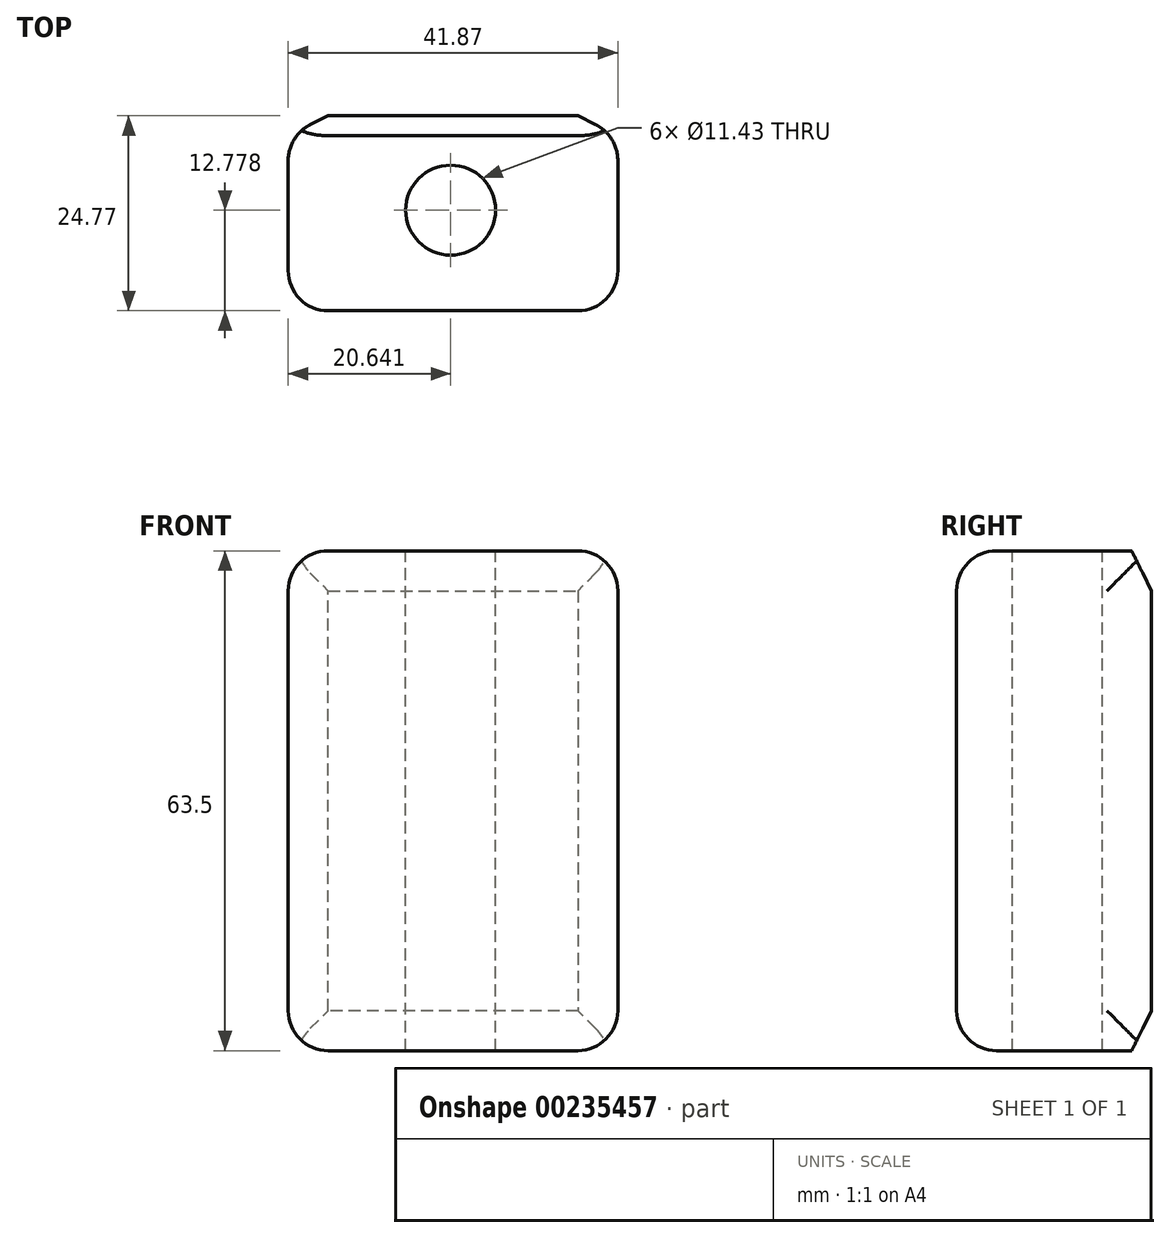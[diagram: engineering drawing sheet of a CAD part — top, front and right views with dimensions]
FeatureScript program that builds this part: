
annotation { "Feature Type Name" : "Feature", "Feature Type Description" : "" }
export const myFeature = defineFeature(function(context is Context, id is Id, definition is map)
    precondition{}
    {
        {
            var Q0;
            Q0=qCreatedBy(makeId("Top.planeOp"),FACE);
            var sketch = newSketch(context, id + "F0", { "sketchPlane" : qUnion([Q0])});
            skLineSegment(sketch, "E0.bottom", {"start": v(0, 0) * mm, "end": v(41.87, 0) * mm});
            skLineSegment(sketch, "E0.top", {"start": v(0, 24.77) * mm, "end": v(41.87, 24.77) * mm});
            skLineSegment(sketch, "E0.left", {"start": v(0, 0) * mm, "end": v(0, 24.77) * mm});
            skLineSegment(sketch, "E0.right", {"start": v(41.87, 0) * mm, "end": v(41.87, 24.77) * mm});
            skSolve(sketch);
        }
        {
            var Q0;
            Q0 = qSketchRegion(id + "F0", true);
            extrude(context, id + "F1", {"entities" : qUnion([Q0]), "depth" : 63.5 * mm});
        }
        {
            var Q0;
            Q0=makeQuery(id+"F1.opExtrude","CAP_FACE",FACE,{"disambiguationData":[OSD([sQuery(id+"F0.wireOp",EDGE,"E0.bottom"),sQuery(id+"F0.wireOp",EDGE,"E0.top"),sQuery(id+"F0.wireOp",EDGE,"E0.left"),sQuery(id+"F0.wireOp",EDGE,"E0.right")])],"isStart":false});
            var sketch = newSketch(context, id + "F2", { "sketchPlane" : qUnion([Q0])});
            skCircle(sketch, "E1", {"center": v(20.64, 12.78) * mm, "radius": 6.65 * mm});
            skSolve(sketch);
        }
        {
            var Q0;
            Q0=sQuery(id+"F2.wireOp",VERTEX,"E1.center");
            var Q1;
            Q1=makeQuery(id+"F1.opExtrude","SWEPT_BODY",BODY,{"disambiguationData":[OSD([sQuery(id+"F0.wireOp",EDGE,"E0.bottom"),sQuery(id+"F0.wireOp",EDGE,"E0.top"),sQuery(id+"F0.wireOp",EDGE,"E0.left"),sQuery(id+"F0.wireOp",EDGE,"E0.right")])]});
            hole(context, id + "F3", {"style" : HoleStyle.SIMPLE, "endStyle" : HoleEndStyle.THROUGH, "holeDiameter" : 11.43 * mm, "locations" : qUnion([Q0]), "scope" : qUnion([Q1]), "isTappedThrough" : true});
        }
        {
            var Q0;
            Q0=makeQuery(id+"F1.opExtrude","SWEPT_FACE",FACE,{"disambiguationData":[OSD([sQuery(id+"F0.wireOp",EDGE,"E0.top")])]});
            chamfer(context, id + "F4", {"entities" : qUnion([Q0]), "chamferType" : ChamferType.TWO_OFFSETS, "width1" : 2.54 * mm, "oppositeDirection" : false, "width2" : 5.08 * mm, "tangentPropagation" : true});
        }
        {
            var Q0;
            Q0=makeQuery(id+"F1.opExtrude","SWEPT_FACE",FACE,{"disambiguationData":[OSD([sQuery(id+"F0.wireOp",EDGE,"E0.bottom")])]});
            fillet(context, id + "F5", {"entities" : qUnion([Q0]), "radius" : 5.08 * mm, "tangentPropagation" : true, "allowEdgeOverflow" : false});
        }
        {
            var Q0;
            {var subQ0=sQuery(id+"F0.wireOp",EDGE,"E0.left");Q0=makeQuery(id+"F5.opFillet","BLEND_EDGE",EDGE,{"blendedFrom":[makeQuery(id+"F1.opExtrude","SWEPT_EDGE",EDGE,{"disambiguationData":[OSD([sQuery(id+"F0.wireOp",EDGE,"E0.bottom"),subQ0])]}),makeQuery(id+"F1.opExtrude","SWEPT_FACE",FACE,{"disambiguationData":[OSD([subQ0])]})],"blendedInto":[makeQuery(id+"F1.opExtrude","SWEPT_FACE",FACE,{"disambiguationData":[OSD([subQ0])]})]});}
            var Q1;
            Q1=makeQuery(id+"F1.opExtrude","SWEPT_FACE",FACE,{"disambiguationData":[OSD([sQuery(id+"F0.wireOp",EDGE,"E0.left")])]});
            fillet(context, id + "F6", {"entities" : qUnion([Q0, Q1]), "radius" : 5.08 * mm, "tangentPropagation" : true, "allowEdgeOverflow" : false});
        }
        {
            var Q0;
            Q0=makeQuery(id+"F1.opExtrude","SWEPT_FACE",FACE,{"disambiguationData":[OSD([sQuery(id+"F0.wireOp",EDGE,"E0.right")])]});
            fillet(context, id + "F7", {"entities" : qUnion([Q0]), "radius" : 5.08 * mm, "tangentPropagation" : true, "allowEdgeOverflow" : false});
        }
    });
